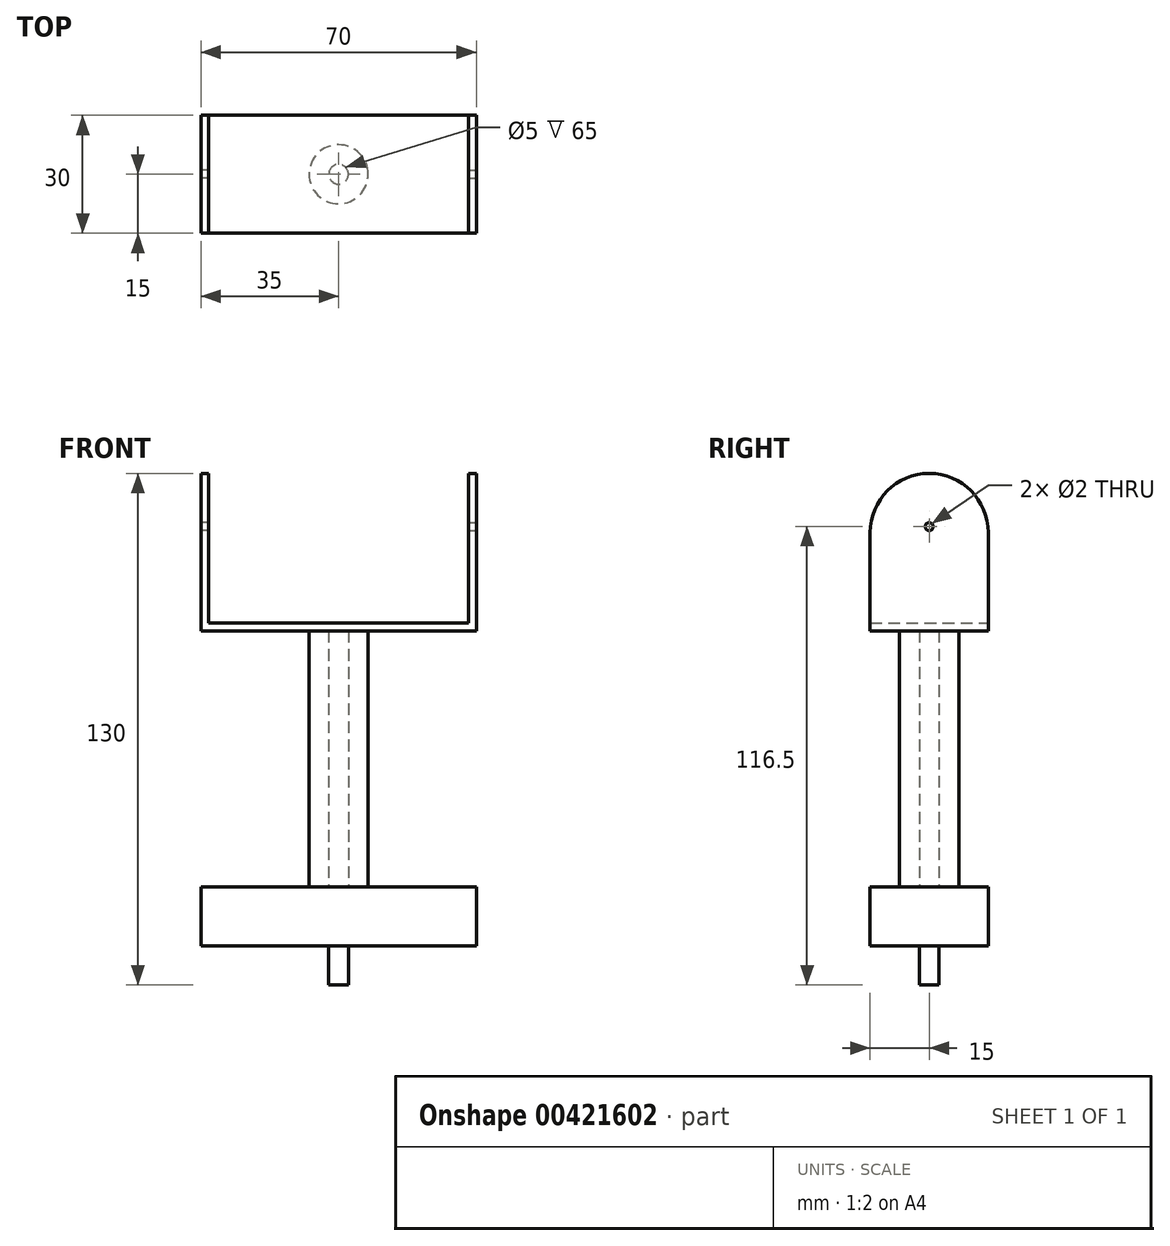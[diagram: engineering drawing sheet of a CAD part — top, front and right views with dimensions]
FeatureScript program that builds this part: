
annotation { "Feature Type Name" : "Feature", "Feature Type Description" : "" }
export const myFeature = defineFeature(function(context is Context, id is Id, definition is map)
    precondition{}
    {
        {
            var Q0;
            Q0=qCreatedBy(makeId("Top.planeOp"),FACE);
            var sketch = newSketch(context, id + "F0", { "sketchPlane" : qUnion([Q0])});
            skCircle(sketch, "E0", {"center": v(0, 0) * mm, "radius": 2.5 * mm});
            skLineSegment(sketch, "E1.bottom", {"start": v(35, 15) * mm, "end": v(-35, 15) * mm});
            skLineSegment(sketch, "E1.top", {"start": v(35, -15) * mm, "end": v(-35, -15) * mm});
            skLineSegment(sketch, "E1.left", {"start": v(35, 15) * mm, "end": v(35, -15) * mm});
            skLineSegment(sketch, "E1.right", {"start": v(-35, 15) * mm, "end": v(-35, -15) * mm});
            skCircle(sketch, "E2", {"center": v(0, 0) * mm, "radius": 7.5 * mm});
            skSolve(sketch);
        }
        {
            var Q0;
            Q0=makeQuery(id+"F0.imprint","IMPRINT",FACE,{"disambiguationData":[TD([[makeQuery(id+"F0.imprint","IMPRINT",EDGE,{"derivedFrom":sQuery(id+"F0.wireOp",EDGE,"E1.bottom")}),1.0]])]});
            var Q1;
            Q1=makeQuery(id+"F0.imprint","IMPRINT",FACE,{"disambiguationData":[TD([[makeQuery(id+"F0.imprint","IMPRINT",EDGE,{"derivedFrom":sQuery(id+"F0.wireOp",EDGE,"E0")}),1.0]])]});
            var Q2;
            Q2=makeQuery(id+"F0.imprint","IMPRINT",FACE,{"disambiguationData":[TD([[makeQuery(id+"F0.imprint","IMPRINT",EDGE,{"derivedFrom":sQuery(id+"F0.wireOp",EDGE,"E0")}),-1.0]])]});
            extrude(context, id + "F1", {"entities" : qUnion([Q0, Q1, Q2]), "depth" : 15 * mm});
        }
        {
            var Q0;
            Q0=makeQuery(id+"F0.imprint","IMPRINT",FACE,{"disambiguationData":[TD([[makeQuery(id+"F0.imprint","IMPRINT",EDGE,{"derivedFrom":sQuery(id+"F0.wireOp",EDGE,"E0")}),1.0]])]});
            extrude(context, id + "F2", {"entities" : qUnion([Q0]), "operationType" : NewBodyOperationType.ADD, "oppositeDirection" : true, "depth" : 10 * mm});
        }
        {
            var Q0;
            Q0=makeQuery(id+"F0.imprint","IMPRINT",FACE,{"disambiguationData":[TD([[makeQuery(id+"F0.imprint","IMPRINT",EDGE,{"derivedFrom":sQuery(id+"F0.wireOp",EDGE,"E0")}),-1.0]])]});
            extrude(context, id + "F3", {"entities" : qUnion([Q0]), "operationType" : NewBodyOperationType.ADD, "depth" : 80 * mm});
        }
        {
            var Q0;
            Q0=makeQuery(id+"F3.opExtrude","CAP_FACE",FACE,{"disambiguationData":[OSD([sQuery(id+"F0.wireOp",EDGE,"E0"),sQuery(id+"F0.wireOp",EDGE,"E2")])],"isStart":false});
            var sketch = newSketch(context, id + "F4", { "sketchPlane" : qUnion([Q0])});
            skLineSegment(sketch, "E3.bottom", {"start": v(35, 15) * mm, "end": v(-35, 15) * mm});
            skLineSegment(sketch, "E3.top", {"start": v(35, -15) * mm, "end": v(-35, -15) * mm});
            skLineSegment(sketch, "E3.left", {"start": v(35, 15) * mm, "end": v(35, -15) * mm});
            skLineSegment(sketch, "E3.right", {"start": v(-35, 15) * mm, "end": v(-35, -15) * mm});
            skPoint(sketch, "E3.middle", {"position": v(0, 0) * mm});
            skLineSegment(sketch, "E4", {"start": v(-33, 15) * mm, "end": v(-33, -15) * mm});
            skLineSegment(sketch, "E5", {"start": v(33, 15) * mm, "end": v(33, -15) * mm});
            skSolve(sketch);
        }
        {
            var Q0;
            {var subQ0=sQuery(id+"F4.wireOp",EDGE,"E4");Q0=makeQuery(id+"F4.imprint","IMPRINT",FACE,{"disambiguationData":[TD([[makeQuery(id+"F4.imprint","IMPRINT",EDGE,{"derivedFrom":subQ0}),1.0]])]});}
            var Q1;
            Q1=makeQuery(id+"F4.imprint","IMPRINT",FACE,{"disambiguationData":[TD([[makeQuery(id+"F4.imprint","IMPRINT",EDGE,{"derivedFrom":makeQuery(id+"F3.opExtrude","CAP_EDGE",EDGE,{"disambiguationData":[OSD([sQuery(id+"F0.wireOp",EDGE,"E0")])],"isStart":false})}),-1.0]])]});
            var Q2;
            Q2=makeQuery(id+"F4.imprint","IMPRINT",FACE,{"disambiguationData":[TD([[makeQuery(id+"F4.imprint","IMPRINT",EDGE,{"derivedFrom":makeQuery(id+"F3.opExtrude","CAP_EDGE",EDGE,{"disambiguationData":[OSD([sQuery(id+"F0.wireOp",EDGE,"E0")])],"isStart":false})}),1.0]])]});
            var Q3;
            {var subQ0=sQuery(id+"F4.wireOp",EDGE,"E3.right");Q3=makeQuery(id+"F4.imprint","IMPRINT",FACE,{"disambiguationData":[TD([[makeQuery(id+"F4.imprint","IMPRINT",EDGE,{"derivedFrom":subQ0}),1.0]])]});}
            var Q4;
            {var subQ0=sQuery(id+"F4.wireOp",EDGE,"E3.left");Q4=makeQuery(id+"F4.imprint","IMPRINT",FACE,{"disambiguationData":[TD([[makeQuery(id+"F4.imprint","IMPRINT",EDGE,{"derivedFrom":subQ0}),-1.0]])]});}
            extrude(context, id + "F5", {"entities" : qUnion([Q0, Q1, Q2, Q3, Q4]), "operationType" : NewBodyOperationType.ADD, "depth" : 2 * mm});
        }
        {
            var Q0;
            {var subQ0=sQuery(id+"F4.wireOp",EDGE,"E3.right");Q0=makeQuery(id+"F4.imprint","IMPRINT",FACE,{"disambiguationData":[TD([[makeQuery(id+"F4.imprint","IMPRINT",EDGE,{"derivedFrom":subQ0}),1.0]])]});}
            var Q1;
            {var subQ0=sQuery(id+"F4.wireOp",EDGE,"E3.left");Q1=makeQuery(id+"F4.imprint","IMPRINT",FACE,{"disambiguationData":[TD([[makeQuery(id+"F4.imprint","IMPRINT",EDGE,{"derivedFrom":subQ0}),-1.0]])]});}
            extrude(context, id + "F6", {"entities" : qUnion([Q0, Q1]), "operationType" : NewBodyOperationType.ADD, "depth" : 25 * mm});
        }
        {
            var Q0;
            {var subQ0=sQuery(id+"F4.wireOp",EDGE,"E3.right");Q0=makeQuery(id+"F6.boolean.opBoolean","MERGE",FACE,{"derivedFrom":[makeQuery(id+"F5.opExtrude","SWEPT_FACE",FACE,{"disambiguationData":[OSD([subQ0])]}),makeQuery(id+"F6.opExtrude","SWEPT_FACE",FACE,{"disambiguationData":[OSD([subQ0])]})]});}
            var sketch = newSketch(context, id + "F7", { "sketchPlane" : qUnion([Q0])});
            skArc(sketch, "E6", {"start": v(15, 105) * mm, "mid": v(0, 120) * mm, "end": v(-15, 105) * mm});
            skCircle(sketch, "E7", {"center": v(0, 106.5) * mm, "radius": 1 * mm});
            skSolve(sketch);
        }
        {
            var Q0;
            Q0=makeQuery(id+"F7.imprint","IMPRINT",FACE,{"disambiguationData":[TD([[makeQuery(id+"F7.imprint","IMPRINT",EDGE,{"derivedFrom":sQuery(id+"F7.wireOp",EDGE,"E6")}),1.0]])]});
            extrude(context, id + "F8", {"entities" : qUnion([Q0]), "operationType" : NewBodyOperationType.ADD, "oppositeDirection" : true, "depth" : 2 * mm});
        }
        {
            var Q0;
            {var subQ0=sQuery(id+"F4.wireOp",EDGE,"E3.left");Q0=makeQuery(id+"F6.boolean.opBoolean","MERGE",FACE,{"derivedFrom":[makeQuery(id+"F5.opExtrude","SWEPT_FACE",FACE,{"disambiguationData":[OSD([subQ0])]}),makeQuery(id+"F6.opExtrude","SWEPT_FACE",FACE,{"disambiguationData":[OSD([subQ0])]})]});}
            var sketch = newSketch(context, id + "F9", { "sketchPlane" : qUnion([Q0])});
            skArc(sketch, "E8", {"start": v(15, 105) * mm, "mid": v(0, 120) * mm, "end": v(-15, 105) * mm});
            skCircle(sketch, "E9", {"center": v(0, 106.5) * mm, "radius": 1 * mm});
            skSolve(sketch);
        }
        {
            var Q0;
            Q0=makeQuery(id+"F9.imprint","IMPRINT",FACE,{"disambiguationData":[TD([[makeQuery(id+"F9.imprint","IMPRINT",EDGE,{"derivedFrom":sQuery(id+"F9.wireOp",EDGE,"E8")}),1.0]])]});
            extrude(context, id + "F10", {"entities" : qUnion([Q0]), "operationType" : NewBodyOperationType.ADD, "oppositeDirection" : true, "depth" : 2 * mm});
        }
    });
